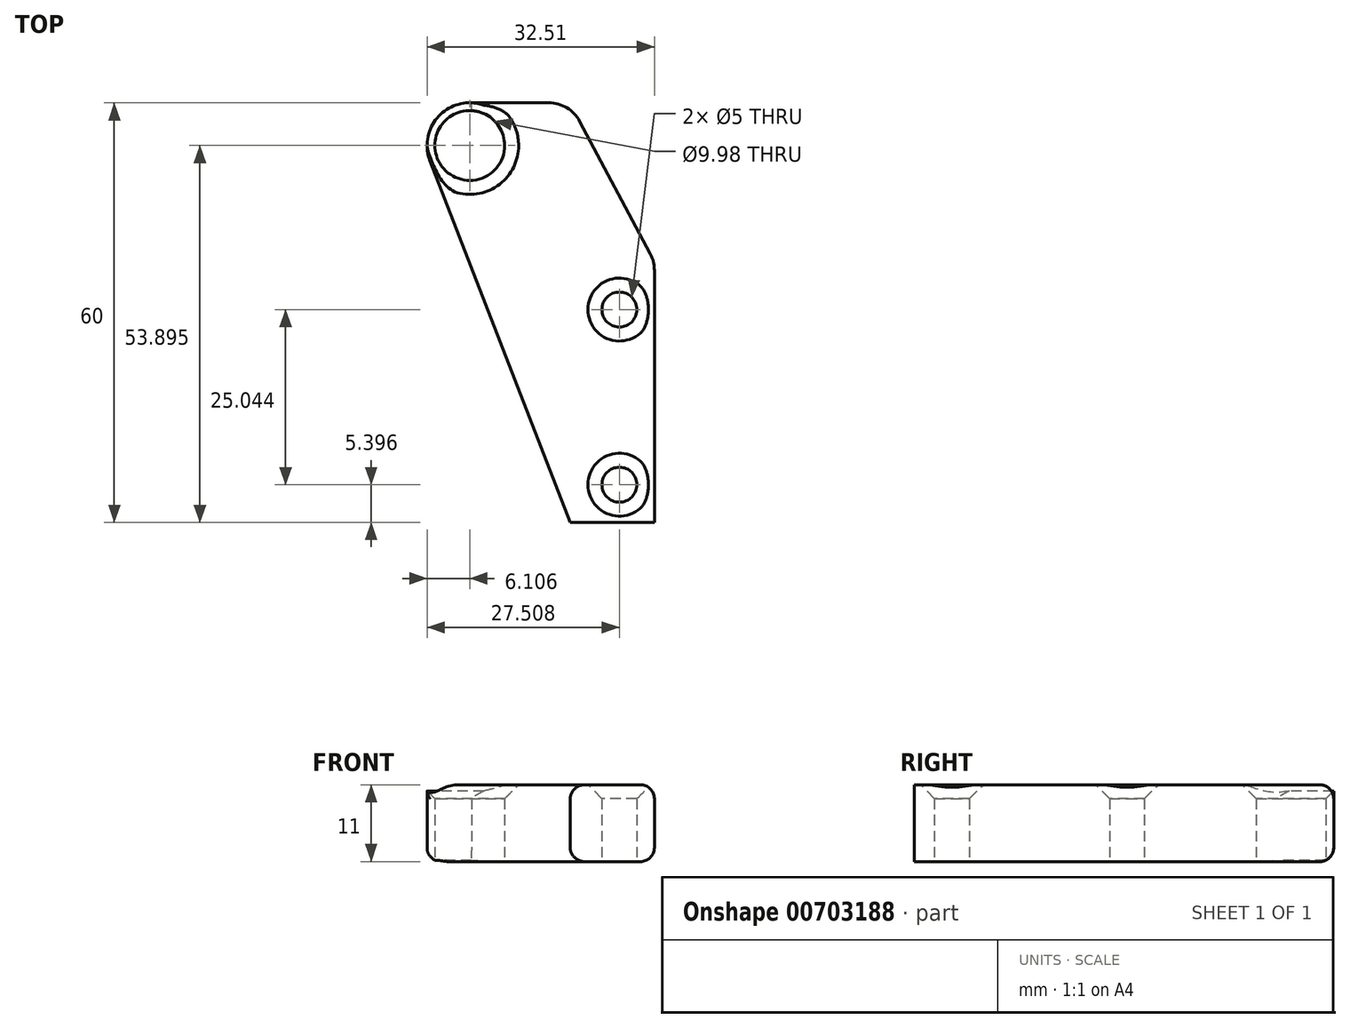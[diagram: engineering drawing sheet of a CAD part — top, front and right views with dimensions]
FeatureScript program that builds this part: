
annotation { "Feature Type Name" : "Feature", "Feature Type Description" : "" }
export const myFeature = defineFeature(function(context is Context, id is Id, definition is map)
    precondition{}
    {
        {
            var Q0;
            Q0=qCreatedBy(makeId("Top.planeOp"),FACE);
            var sketch = newSketch(context, id + "F0", { "sketchPlane" : qUnion([Q0])});
            skLineSegment(sketch, "E0.top", {"start": v(12.03, 0) * mm, "end": v(0, 0) * mm});
            skLineSegment(sketch, "E0.left", {"start": v(12.03, 37.33) * mm, "end": v(12.03, 0) * mm});
            skLineSegment(sketch, "E1.bottom", {"start": v(-0.07, 60) * mm, "end": v(-14.13, 60) * mm});
            skLineSegment(sketch, "E2", {"start": v(-20.07, 51.68) * mm, "end": v(0, 0) * mm});
            skLineSegment(sketch, "E3", {"start": v(-0.07, 60) * mm, "end": v(12.03, 37.33) * mm});
            skArc(sketch, "E4", {"start": v(-14.13, 60) * mm, "mid": v(-19.35, 57.44) * mm, "end": v(-20.07, 51.68) * mm});
            skPoint(sketch, "E1.right.start.orphan", {"position": v(-20.07, 60) * mm});
            skCircle(sketch, "E5", {"center": v(-14.37, 53.9) * mm, "radius": 5 * mm});
            skCircle(sketch, "E6", {"center": v(7.03, 5.4) * mm, "radius": 2.5 * mm});
            skCircle(sketch, "E7", {"center": v(7.03, 30.44) * mm, "radius": 2.5 * mm});
            skSolve(sketch);
        }
        {
            var Q0;
            Q0 = qSketchRegion(id + "F0", true);
            extrude(context, id + "F1", {"entities" : qUnion([Q0]), "depth" : 11 * mm, "offsetDistance" : 25 * mm});
        }
        {
            var Q0;
            Q0=makeQuery(id+"F1.opExtrude","SWEPT_EDGE",EDGE,{"disambiguationData":[OSD([sQuery(id+"F0.wireOp",EDGE,"E1.bottom"),sQuery(id+"F0.wireOp",EDGE,"E3")])]});
            var Q1;
            Q1=makeQuery(id+"F1.opExtrude","SWEPT_EDGE",EDGE,{"disambiguationData":[OSD([sQuery(id+"F0.wireOp",EDGE,"E0.left"),sQuery(id+"F0.wireOp",EDGE,"E3")])]});
            fillet(context, id + "F2", {"entities" : qUnion([Q0, Q1]), "radius" : 5 * mm, "tangentPropagation" : true, "allowEdgeOverflow" : false});
        }
        {
            var Q0;
            Q0=makeQuery(id+"F1.opExtrude","CAP_EDGE",EDGE,{"disambiguationData":[OSD([sQuery(id+"F0.wireOp",EDGE,"E5")])],"isStart":false});
            var Q1;
            Q1=makeQuery(id+"F1.opExtrude","CAP_EDGE",EDGE,{"disambiguationData":[OSD([sQuery(id+"F0.wireOp",EDGE,"E7")])],"isStart":false});
            var Q2;
            Q2=makeQuery(id+"F1.opExtrude","CAP_EDGE",EDGE,{"disambiguationData":[OSD([sQuery(id+"F0.wireOp",EDGE,"E6")])],"isStart":false});
            chamfer(context, id + "F3", {"entities" : qUnion([Q0, Q1, Q2]), "width" : 2 * mm, "tangentPropagation" : true});
        }
        {
            var Q0;
            Q0=makeQuery(id+"F1.opExtrude","CAP_EDGE",EDGE,{"disambiguationData":[OSD([sQuery(id+"F0.wireOp",EDGE,"E2")])],"isStart":false});
            var Q1;
            Q1=makeQuery(id+"F1.opExtrude","CAP_EDGE",EDGE,{"disambiguationData":[OSD([sQuery(id+"F0.wireOp",EDGE,"E0.left")])],"isStart":false});
            var Q2;
            Q2=makeQuery(id+"F1.opExtrude","CAP_EDGE",EDGE,{"disambiguationData":[OSD([sQuery(id+"F0.wireOp",EDGE,"E2")])],"isStart":true});
            var Q3;
            Q3=makeQuery(id+"F1.opExtrude","CAP_EDGE",EDGE,{"disambiguationData":[OSD([sQuery(id+"F0.wireOp",EDGE,"E3")])],"isStart":true});
            fillet(context, id + "F4", {"entities" : qUnion([Q0, Q1, Q2, Q3]), "tangentPropagation" : true, "radius" : 2 * mm, "defaultsChanged" : false, "vertexSettings" : [], "allowEdgeOverflow" : false});
        }
    });
